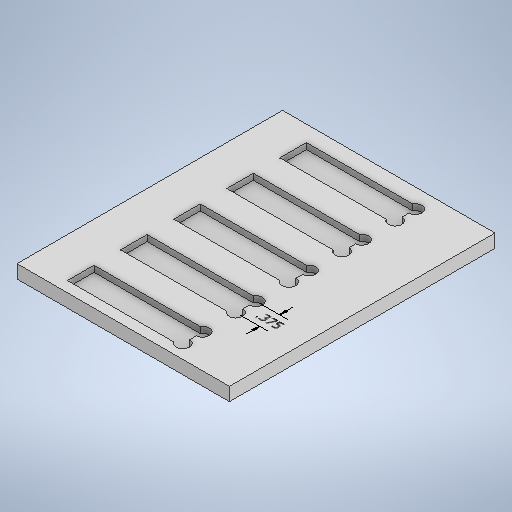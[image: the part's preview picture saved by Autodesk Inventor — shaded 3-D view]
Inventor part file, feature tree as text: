
AUTODESK INVENTOR PART (.ipt)
format: ipt  version: 2025.3 (Build 293356030, 356C)  size: 284,160 bytes
history: native  units: in
note: dims shown in document units (in); Inventor stores cm internally (conversion verified against a paired STEP export)
features: sketch x3, other x2, extrude x2
ambient origin geometry x8: Origin, YZ Plane, XZ Plane, XY Plane, X Axis, Y Axis, Z Axis, Center Point
bodies: Solid1 (feature_tree)
feature tree (7):
  other  "Annotations"
  extrude  "Extrusion1"  Depth=5.0in
  extrude  "Extrusion2"  Depth=0.5in
  sketch  "Sketch1"  dims[d0=4.0in d1=5.0in]
  sketch  "Sketch2"  dims[d6=0.25in d7=0.25in d8=0.125in d9=2.0in d10=0.75in d11=0.2in d12=1.9685in d14=1.0in d15=0.3937in d17=1.0in d19=0.115in d20=0.0in d21=0.3747in]
  sketch  "Sketch Rectangular Pattern1"  dims[d2=0.25in d3=0.0in d5=0.5in]
  other  "Linear Dimension 1"
